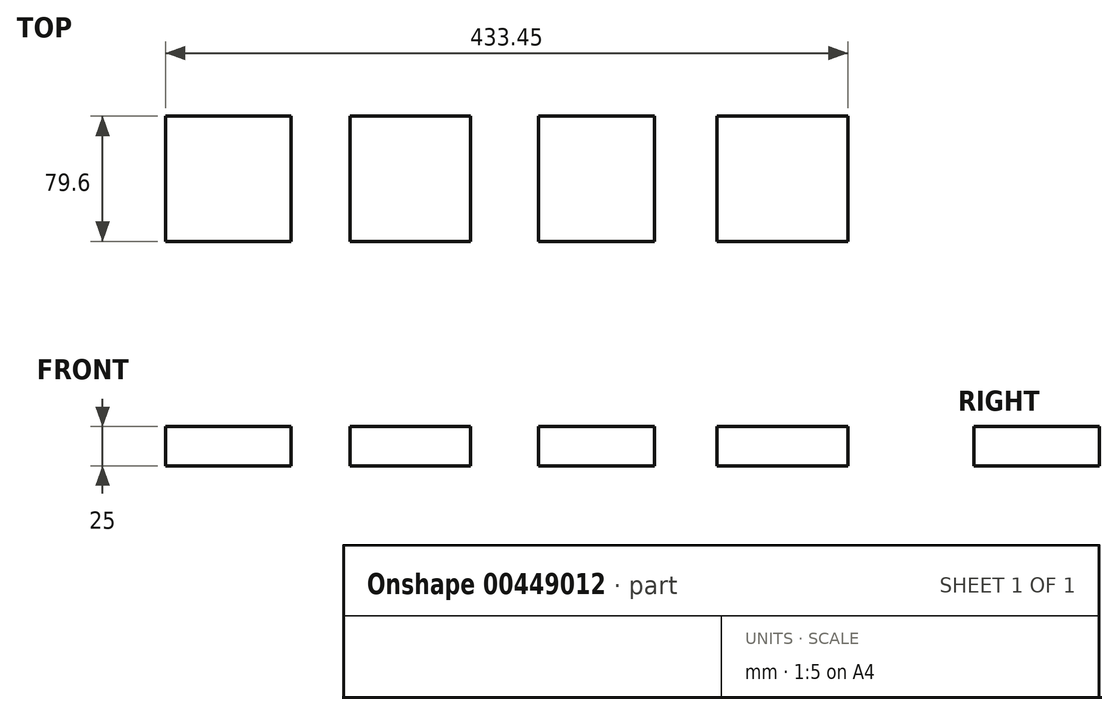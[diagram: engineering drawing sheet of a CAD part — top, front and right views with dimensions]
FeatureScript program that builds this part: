
annotation { "Feature Type Name" : "Feature", "Feature Type Description" : "" }
export const myFeature = defineFeature(function(context is Context, id is Id, definition is map)
    precondition{}
    {
        {
            var Q0;
            Q0=qCreatedBy(makeId("Top.planeOp"),FACE);
            var sketch = newSketch(context, id + "F0", { "sketchPlane" : qUnion([Q0])});
            skLineSegment(sketch, "E0.bottom", {"start": v(-39.8, 39.8) * mm, "end": v(39.8, 39.8) * mm});
            skLineSegment(sketch, "E0.top", {"start": v(-39.8, -39.8) * mm, "end": v(39.8, -39.8) * mm});
            skLineSegment(sketch, "E0.left", {"start": v(-39.8, 39.8) * mm, "end": v(-39.8, -39.8) * mm});
            skLineSegment(sketch, "E0.right", {"start": v(39.8, 39.8) * mm, "end": v(39.8, -39.8) * mm});
            skPoint(sketch, "E0.middle", {"position": v(0, 0) * mm});
            skLineSegment(sketch, "E1.bottom", {"start": v(77.43, 39.8) * mm, "end": v(153.77, 39.8) * mm});
            skLineSegment(sketch, "E1.top", {"start": v(77.43, -39.8) * mm, "end": v(153.77, -39.8) * mm});
            skLineSegment(sketch, "E1.left", {"start": v(77.43, 39.8) * mm, "end": v(77.43, -39.8) * mm});
            skLineSegment(sketch, "E1.right", {"start": v(153.77, 39.8) * mm, "end": v(153.77, -39.8) * mm});
            skPoint(sketch, "E1.middle", {"position": v(115.6, 0) * mm});
            skLineSegment(sketch, "E2.bottom", {"start": v(197, 39.8) * mm, "end": v(270.75, 39.8) * mm});
            skLineSegment(sketch, "E2.top", {"start": v(197, -39.8) * mm, "end": v(270.75, -39.8) * mm});
            skLineSegment(sketch, "E2.left", {"start": v(197, 39.8) * mm, "end": v(197, -39.8) * mm});
            skLineSegment(sketch, "E2.right", {"start": v(270.75, 39.8) * mm, "end": v(270.75, -39.8) * mm});
            skPoint(sketch, "E2.middle", {"position": v(233.87, 0) * mm});
            skLineSegment(sketch, "E3.bottom", {"start": v(310.29, 39.8) * mm, "end": v(393.65, 39.8) * mm});
            skLineSegment(sketch, "E3.top", {"start": v(310.29, -39.8) * mm, "end": v(393.65, -39.8) * mm});
            skLineSegment(sketch, "E3.left", {"start": v(310.29, 39.8) * mm, "end": v(310.29, -39.8) * mm});
            skLineSegment(sketch, "E3.right", {"start": v(393.65, 39.8) * mm, "end": v(393.65, -39.8) * mm});
            skPoint(sketch, "E3.middle", {"position": v(351.97, 0) * mm});
            skSolve(sketch);
        }
        {
            var Q0;
            Q0=qSketchRegion(id+"F0",true);
            extrude(context, id + "F1", {"entities" : qUnion([Q0]), "depth" : 25 * mm});
        }
    });
